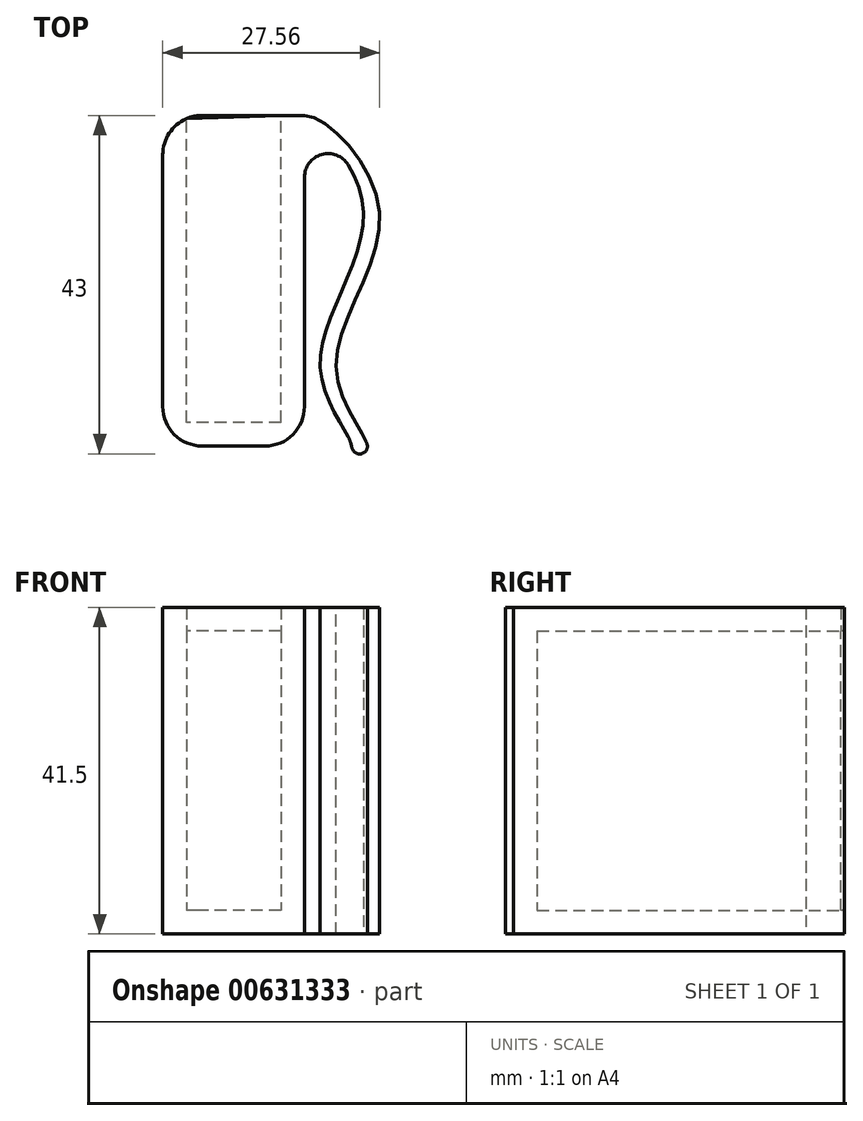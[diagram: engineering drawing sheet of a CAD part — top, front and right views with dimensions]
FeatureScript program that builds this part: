
annotation { "Feature Type Name" : "Feature", "Feature Type Description" : "" }
export const myFeature = defineFeature(function(context is Context, id is Id, definition is map)
    precondition{}
    {
        {
            var Q0;
            Q0=qCreatedBy(makeId("Top.planeOp"),FACE);
            var sketch = newSketch(context, id + "F0", { "sketchPlane" : qUnion([Q0])});
            skLineSegment(sketch, "E0", {"start": v(7, 0) * mm, "end": v(7, 42) * mm});
            skLineSegment(sketch, "E1", {"start": v(10, 0) * mm, "end": v(10, 40) * mm});
            skFitSpline(sketch, "E2", {"points": [v(10, 40) * mm, v(17.5, 30) * mm, v(12, 10) * mm, v(16, 0) * mm], "startDerivative": vector(27.5, 0) * mm, "endDerivative": vector(2.01, -15.72) * mm});
            skFitSpline(sketch, "E3", {"points": [v(10, 42) * mm, v(19.5, 30) * mm, v(14, 10) * mm, v(18, 0) * mm], "startDerivative": vector(25.68, 0) * mm, "endDerivative": vector(2.08, -16.24) * mm});
            skLineSegment(sketch, "E4.top", {"start": v(7, 42) * mm, "end": v(10, 42) * mm});
            skLineSegment(sketch, "E5", {"start": v(16, 0) * mm, "end": v(18, 0) * mm});
            skCircle(sketch, "E6", {"center": v(17, 0) * mm, "radius": 1 * mm});
            skLineSegment(sketch, "E7", {"start": v(10, 0) * mm, "end": v(7, 0) * mm});
            skLineSegment(sketch, "E8.bottom", {"start": v(7, 0) * mm, "end": v(-5, 0) * mm});
            skLineSegment(sketch, "E8.top", {"start": v(7, 3) * mm, "end": v(-5, 3) * mm});
            skLineSegment(sketch, "E8.left", {"start": v(7, 0) * mm, "end": v(7, 3) * mm});
            skLineSegment(sketch, "E8.right", {"start": v(-5, 0) * mm, "end": v(-5, 3) * mm});
            skLineSegment(sketch, "E9.bottom", {"start": v(-5, 0) * mm, "end": v(-8, 0) * mm});
            skLineSegment(sketch, "E9.top", {"start": v(-5, 42) * mm, "end": v(-8, 42) * mm});
            skLineSegment(sketch, "E9.left", {"start": v(-5, 0) * mm, "end": v(-5, 42) * mm});
            skLineSegment(sketch, "E9.right", {"start": v(-8, 0) * mm, "end": v(-8, 42) * mm});
            skLineSegment(sketch, "E10", {"start": v(7, 42) * mm, "end": v(-5, 42) * mm});
            skSolve(sketch);
        }
        {
            var Q0;
            {var subQ0=sQuery(id+"F0.wireOp",EDGE,"E5");Q0=makeQuery(id+"F0.imprint","IMPRINT",FACE,{"disambiguationData":[TD([[makeQuery(id+"F0.imprint","IMPRINT",EDGE,{"derivedFrom":subQ0}),-1.0]])]});}
            var Q1;
            {var subQ1=sQuery(id+"F0.wireOp",EDGE,"E5");Q1=makeQuery(id+"F0.imprint","IMPRINT",FACE,{"disambiguationData":[TD([[makeQuery(id+"F0.imprint","IMPRINT",EDGE,{"derivedFrom":subQ1}),1.0]])]});}
            var Q2;
            Q2=makeQuery(id+"F0.imprint","IMPRINT",FACE,{"disambiguationData":[TD([[makeQuery(id+"F0.imprint","IMPRINT",EDGE,{"derivedFrom":sQuery(id+"F0.wireOp",EDGE,"E0")}),-1.0]])]});
            var Q3;
            Q3=makeQuery(id+"F0.imprint","IMPRINT",FACE,{"disambiguationData":[TD([[makeQuery(id+"F0.imprint","IMPRINT",EDGE,{"derivedFrom":sQuery(id+"F0.wireOp",EDGE,"E8.bottom")}),-1.0]])]});
            var Q4;
            {var subQ3=sQuery(id+"F0.wireOp",EDGE,"E9.bottom");Q4=makeQuery(id+"F0.imprint","IMPRINT",FACE,{"disambiguationData":[TD([[makeQuery(id+"F0.imprint","IMPRINT",EDGE,{"derivedFrom":subQ3}),-1.0]])]});}
            extrude(context, id + "F1", {"entities" : qUnion([Q0, Q1, Q2, Q3, Q4]), "depth" : 35.5 * mm, "offsetDistance" : 25 * mm});
        }
        {
            var Q0;
            {var subQ3=sQuery(id+"F0.wireOp",EDGE,"E9.bottom");Q0=makeQuery(id+"F0.imprint","IMPRINT",FACE,{"disambiguationData":[TD([[makeQuery(id+"F0.imprint","IMPRINT",EDGE,{"derivedFrom":subQ3}),-1.0]])]});}
            var Q1;
            Q1=makeQuery(id+"F0.imprint","IMPRINT",FACE,{"disambiguationData":[TD([[makeQuery(id+"F0.imprint","IMPRINT",EDGE,{"derivedFrom":sQuery(id+"F0.wireOp",EDGE,"E0")}),-1.0]])]});
            var Q2;
            {var subQ0=sQuery(id+"F0.wireOp",EDGE,"E5");Q2=makeQuery(id+"F0.imprint","IMPRINT",FACE,{"disambiguationData":[TD([[makeQuery(id+"F0.imprint","IMPRINT",EDGE,{"derivedFrom":subQ0}),-1.0]])]});}
            var Q3;
            {var subQ1=sQuery(id+"F0.wireOp",EDGE,"E5");Q3=makeQuery(id+"F0.imprint","IMPRINT",FACE,{"disambiguationData":[TD([[makeQuery(id+"F0.imprint","IMPRINT",EDGE,{"derivedFrom":subQ1}),1.0]])]});}
            var Q4;
            Q4=makeQuery(id+"F0.imprint","IMPRINT",FACE,{"disambiguationData":[TD([[makeQuery(id+"F0.imprint","IMPRINT",EDGE,{"derivedFrom":sQuery(id+"F0.wireOp",EDGE,"E0")}),1.0]])]});
            var Q5;
            {var subQ0=sQuery(id+"F0.wireOp",EDGE,"E8.bottom");Q5=makeQuery(id+"F0.imprint","IMPRINT",FACE,{"disambiguationData":[TD([[makeQuery(id+"F0.imprint","IMPRINT",EDGE,{"derivedFrom":subQ0}),-1.0]])]});}
            extrude(context, id + "F2", {"entities" : qUnion([Q0, Q1, Q2, Q3, Q4, Q5]), "operationType" : NewBodyOperationType.ADD, "depth" : -3 * mm, "offsetDistance" : 25 * mm});
        }
        {
            var Q0;
            Q0=makeQuery(id+"F1.opExtrude","SWEPT_EDGE",EDGE,{"disambiguationData":[OSD([sQuery(id+"F0.wireOp",EDGE,"E3"),sQuery(id+"F0.wireOp",EDGE,"E4.top")])]});
            var Q1;
            Q1=makeQuery(id+"F1.opExtrude","SWEPT_EDGE",EDGE,{"disambiguationData":[OSD([sQuery(id+"F0.wireOp",EDGE,"2s26rBtf-RWpX-GKQd-BOM7-meuTIu4NusW0"),sQuery(id+"F0.wireOp",EDGE,"3TBNVrqH-agQP-zHz2-TEnJ-zR4mGGCQUChH")])]});
            var Q2;
            Q2=makeQuery(id+"F1.opExtrude","SWEPT_EDGE",EDGE,{"disambiguationData":[OSD([sQuery(id+"F0.wireOp",EDGE,"E1"),sQuery(id+"F0.wireOp",EDGE,"E2")])]});
            fillet(context, id + "F3", {"entities" : qUnion([Q0, Q1, Q2]), "radius" : 3 * mm, "tangentPropagation" : true, "allowEdgeOverflow" : false});
        }
        {
            var Q0;
            Q0=makeQuery(id+"F1.opExtrude","SWEPT_EDGE",EDGE,{"disambiguationData":[OSD([sQuery(id+"F0.wireOp",EDGE,"uS0RZwKG-Npmu-du4L-n6SU-w1RPvIbTGl1z"),sQuery(id+"F0.wireOp",EDGE,"u5OqRpMJ-uTdK-0PYW-wHET-1gvOn3WCqaQb")])]});
            var Q1;
            Q1=makeQuery(id+"F1.opExtrude","SWEPT_EDGE",EDGE,{"disambiguationData":[OSD([sQuery(id+"F0.wireOp",EDGE,"E2"),sQuery(id+"F0.wireOp",EDGE,"E5"),sQuery(id+"F0.wireOp",EDGE,"E6")])]});
            var Q2;
            Q2=makeQuery(id+"F1.opExtrude","SWEPT_EDGE",EDGE,{"disambiguationData":[OSD([sQuery(id+"F0.wireOp",EDGE,"E1"),sQuery(id+"F0.wireOp",EDGE,"E7")])]});
            var Q3;
            Q3=makeQuery(id+"F1.opExtrude","SWEPT_EDGE",EDGE,{"disambiguationData":[OSD([sQuery(id+"F0.wireOp",EDGE,"E9.top"),sQuery(id+"F0.wireOp",EDGE,"E9.right")])]});
            var Q4;
            {var subQ0=sQuery(id+"F0.wireOp",EDGE,"E9.right");var subQ1=sQuery(id+"F0.wireOp",EDGE,"E9.bottom");Q4=makeQuery(id+"F2.boolean.opBoolean","MERGE",EDGE,{"derivedFrom":[makeQuery(id+"F1.opExtrude","SWEPT_EDGE",EDGE,{"disambiguationData":[OSD([subQ1,subQ0])]}),makeQuery(id+"F2.opExtrude","SWEPT_EDGE",EDGE,{"disambiguationData":[OSD([subQ1,subQ0])]})]});}
            fillet(context, id + "F4", {"entities" : qUnion([Q0, Q1, Q2, Q3, Q4]), "radius" : 5 * mm, "tangentPropagation" : true, "allowEdgeOverflow" : false});
        }
        {
            var Q0;
            Q0=makeQuery(id+"F1.opExtrude","CAP_FACE",FACE,{"disambiguationData":[OSD([sQuery(id+"F0.wireOp",EDGE,"E0"),sQuery(id+"F0.wireOp",EDGE,"E1"),sQuery(id+"F0.wireOp",EDGE,"E2"),sQuery(id+"F0.wireOp",EDGE,"E3"),sQuery(id+"F0.wireOp",EDGE,"E4.top"),sQuery(id+"F0.wireOp",EDGE,"E6"),sQuery(id+"F0.wireOp",EDGE,"E7"),sQuery(id+"F0.wireOp",EDGE,"E8.bottom"),sQuery(id+"F0.wireOp",EDGE,"E8.top"),sQuery(id+"F0.wireOp",EDGE,"E9.bottom"),sQuery(id+"F0.wireOp",EDGE,"E9.top"),sQuery(id+"F0.wireOp",EDGE,"E9.left"),sQuery(id+"F0.wireOp",EDGE,"E9.right")])],"isStart":false});
            var sketch = newSketch(context, id + "F5", { "sketchPlane" : qUnion([Q0])});
            skLineSegment(sketch, "E11", {"start": v(7, 42) * mm, "end": v(-5, 41.58) * mm});
            skSolve(sketch);
        }
        {
            var Q0;
            {var subQ12=sQuery(id+"F0.wireOp",EDGE,"E0");Q0=makeQuery(id+"F5.imprint","IMPRINT",FACE,{"disambiguationData":[TD([[makeQuery(id+"F5.imprint","IMPRINT",EDGE,{"derivedFrom":makeQuery(id+"F1.opExtrude","CAP_EDGE",EDGE,{"disambiguationData":[OSD([subQ12])],"isStart":false})}),-1.0]])]});}
            var Q1;
            Q1=makeQuery(id+"F5.imprint","IMPRINT",FACE,{"disambiguationData":[TD([[makeQuery(id+"F5.imprint","IMPRINT",EDGE,{"derivedFrom":sQuery(id+"F5.wireOp",EDGE,"E11")}),1.0]])]});
            extrude(context, id + "F6", {"entities" : qUnion([Q0, Q1]), "operationType" : NewBodyOperationType.ADD, "depth" : 3 * mm, "offsetDistance" : 25 * mm});
        }
    });
